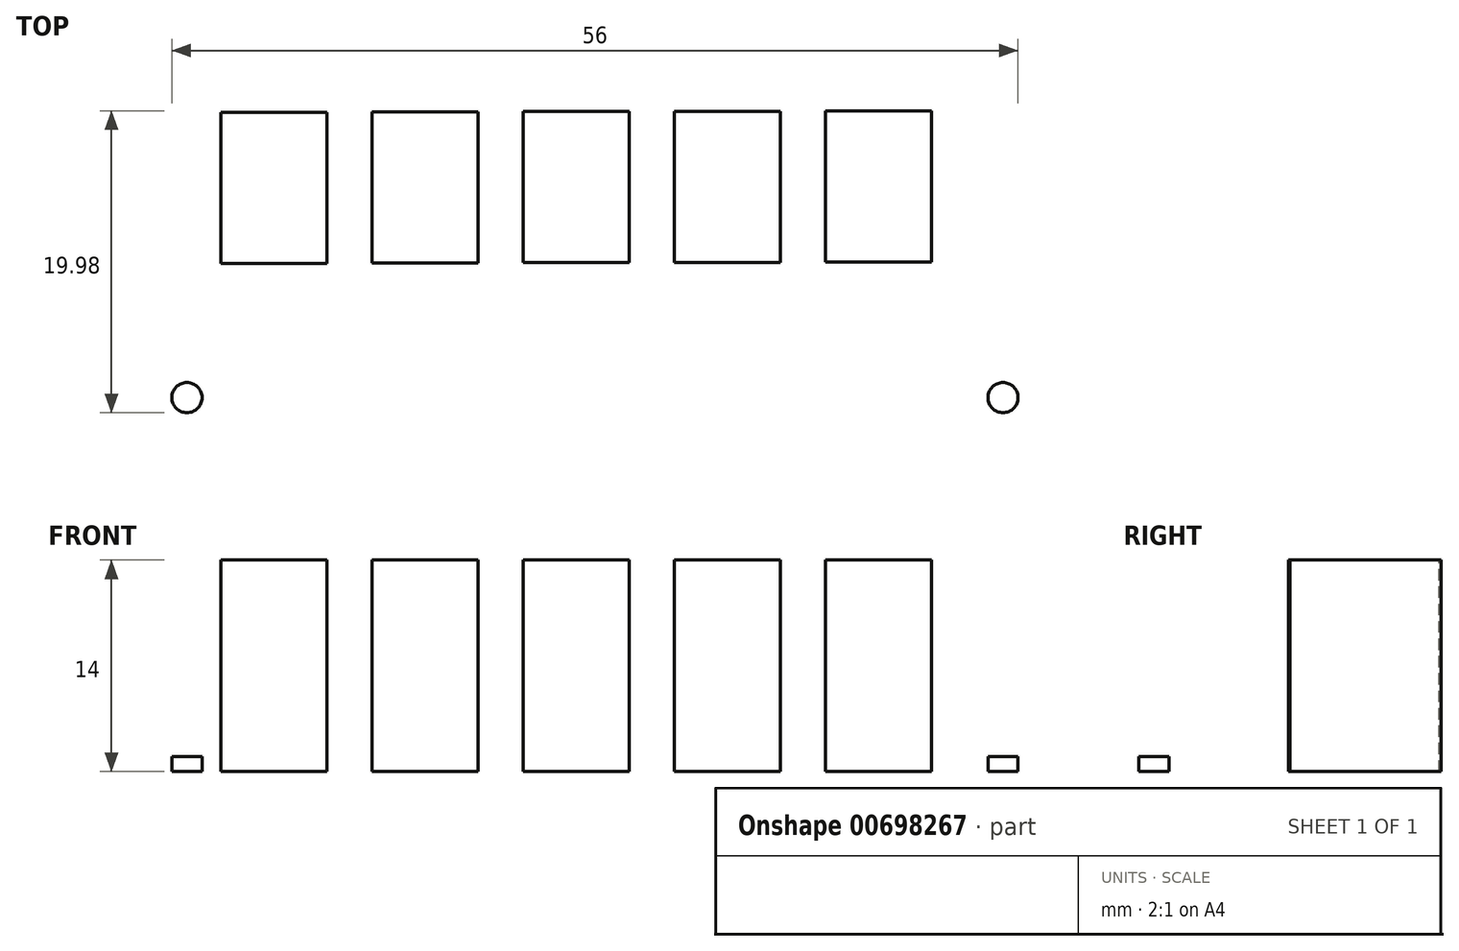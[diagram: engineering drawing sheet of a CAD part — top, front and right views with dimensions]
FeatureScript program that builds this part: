
annotation { "Feature Type Name" : "Feature", "Feature Type Description" : "" }
export const myFeature = defineFeature(function(context is Context, id is Id, definition is map)
    precondition{}
    {
        {
            var Q0;
            Q0=qCreatedBy(makeId("Top.planeOp"),FACE);
            var sketch = newSketch(context, id + "F0", { "sketchPlane" : qUnion([Q0])});
            skLineSegment(sketch, "E0.bottom", {"start": v(29, 19.5) * mm, "end": v(-29, 19.5) * mm});
            skLineSegment(sketch, "E0.top", {"start": v(29, -19.5) * mm, "end": v(-29, -19.5) * mm});
            skLineSegment(sketch, "E0.left", {"start": v(29, 19.5) * mm, "end": v(29, -19.5) * mm});
            skLineSegment(sketch, "E0.right", {"start": v(-29, 19.5) * mm, "end": v(-29, -19.5) * mm});
            skPoint(sketch, "E0.middle", {"position": v(0, 0) * mm});
            skSolve(sketch);
        }
        {
            var Q0;
            Q0 = qSketchRegion(id + "F0", true);
            extrude(context, id + "F1", {"entities" : qUnion([Q0]), "depth" : 14 * mm, "offsetDistance" : 25.4 * mm});
        }
        {
            var Q0;
            Q0=makeQuery(id+"F1.opExtrude","CAP_FACE",FACE,{"disambiguationData":[OSD([sQuery(id+"F0.wireOp",EDGE,"E0.bottom"),sQuery(id+"F0.wireOp",EDGE,"E0.top"),sQuery(id+"F0.wireOp",EDGE,"E0.left"),sQuery(id+"F0.wireOp",EDGE,"E0.right")])],"isStart":false});
            var sketch = newSketch(context, id + "F2", { "sketchPlane" : qUnion([Q0])});
            skLineSegment(sketch, "E1.bottom", {"start": v(-17.74, -8.62) * mm, "end": v(-24.74, -8.62) * mm});
            skLineSegment(sketch, "E1.top", {"start": v(-17.74, 1.38) * mm, "end": v(-24.74, 1.38) * mm});
            skLineSegment(sketch, "E1.left", {"start": v(-17.74, -8.62) * mm, "end": v(-17.74, 1.38) * mm});
            skLineSegment(sketch, "E1.right", {"start": v(-24.74, -8.62) * mm, "end": v(-24.74, 1.38) * mm});
            skPoint(sketch, "E1.middle", {"position": v(-21.24, -3.62) * mm});
            skLineSegment(sketch, "E2.1.0.0", {"start": v(-7.74, -8.6) * mm, "end": v(-7.74, 1.4) * mm});
            skLineSegment(sketch, "E2.1.0.1", {"start": v(-7.74, 1.4) * mm, "end": v(-14.74, 1.4) * mm});
            skLineSegment(sketch, "E2.1.0.2", {"start": v(-14.74, -8.6) * mm, "end": v(-14.74, 1.4) * mm});
            skLineSegment(sketch, "E2.1.0.3", {"start": v(-7.74, -8.6) * mm, "end": v(-14.74, -8.6) * mm});
            skLineSegment(sketch, "E2.2.0.0", {"start": v(2.26, -8.57) * mm, "end": v(2.26, 1.43) * mm});
            skLineSegment(sketch, "E2.2.0.1", {"start": v(2.26, 1.43) * mm, "end": v(-4.74, 1.43) * mm});
            skLineSegment(sketch, "E2.2.0.2", {"start": v(-4.74, -8.57) * mm, "end": v(-4.74, 1.43) * mm});
            skLineSegment(sketch, "E2.2.0.3", {"start": v(2.26, -8.57) * mm, "end": v(-4.74, -8.57) * mm});
            skLineSegment(sketch, "E2.3.0.0", {"start": v(12.26, -8.54) * mm, "end": v(12.26, 1.46) * mm});
            skLineSegment(sketch, "E2.3.0.1", {"start": v(12.26, 1.46) * mm, "end": v(5.26, 1.46) * mm});
            skLineSegment(sketch, "E2.3.0.2", {"start": v(5.26, -8.54) * mm, "end": v(5.26, 1.46) * mm});
            skLineSegment(sketch, "E2.3.0.3", {"start": v(12.26, -8.54) * mm, "end": v(5.26, -8.54) * mm});
            skLineSegment(sketch, "E2.4.0.0", {"start": v(22.26, -8.52) * mm, "end": v(22.26, 1.48) * mm});
            skLineSegment(sketch, "E2.4.0.1", {"start": v(22.26, 1.48) * mm, "end": v(15.26, 1.48) * mm});
            skLineSegment(sketch, "E2.4.0.2", {"start": v(15.26, -8.52) * mm, "end": v(15.26, 1.48) * mm});
            skLineSegment(sketch, "E2.4.0.3", {"start": v(22.26, -8.52) * mm, "end": v(15.26, -8.52) * mm});
            skLineSegment(sketch, "E2.direction1", {"start": v(-17.74, -8.62) * mm, "end": v(-7.74, -8.6) * mm, "construction": true});
            skSolve(sketch);
        }
        {
            var Q0;
            Q0=makeQuery(id+"F2.imprint","IMPRINT",FACE,{"disambiguationData":[TD([[makeQuery(id+"F2.imprint","IMPRINT",EDGE,{"derivedFrom":sQuery(id+"F2.wireOp",EDGE,"E1.bottom")}),1.0]])]});
            extrude(context, id + "F3", {"entities" : qUnion([Q0]), "operationType" : NewBodyOperationType.REMOVE, "oppositeDirection" : true, "depth" : 13 * mm, "offsetDistance" : 25 * mm});
        }
        {
            var Q0;
            Q0=makeQuery(id+"F3.boolean.opBoolean","COPY",FACE,{"derivedFrom":makeQuery(id+"F3.opExtrude","CAP_FACE",FACE,{"disambiguationData":[OSD([sQuery(id+"F0.wireOp",EDGE,"E0.bottom"),sQuery(id+"F0.wireOp",EDGE,"E0.top"),sQuery(id+"F0.wireOp",EDGE,"E0.left"),sQuery(id+"F0.wireOp",EDGE,"E0.right"),sQuery(id+"F2.wireOp",EDGE,"E1.bottom"),sQuery(id+"F2.wireOp",EDGE,"E1.top"),sQuery(id+"F2.wireOp",EDGE,"E1.left"),sQuery(id+"F2.wireOp",EDGE,"E1.right"),sQuery(id+"F2.wireOp",EDGE,"E2.1.0.0"),sQuery(id+"F2.wireOp",EDGE,"E2.1.0.1"),sQuery(id+"F2.wireOp",EDGE,"E2.1.0.2"),sQuery(id+"F2.wireOp",EDGE,"E2.1.0.3"),sQuery(id+"F2.wireOp",EDGE,"E2.2.0.0"),sQuery(id+"F2.wireOp",EDGE,"E2.2.0.1"),sQuery(id+"F2.wireOp",EDGE,"E2.2.0.2"),sQuery(id+"F2.wireOp",EDGE,"E2.2.0.3"),sQuery(id+"F2.wireOp",EDGE,"E2.3.0.0"),sQuery(id+"F2.wireOp",EDGE,"E2.3.0.1"),sQuery(id+"F2.wireOp",EDGE,"E2.3.0.2"),sQuery(id+"F2.wireOp",EDGE,"E2.3.0.3"),sQuery(id+"F2.wireOp",EDGE,"E2.4.0.0"),sQuery(id+"F2.wireOp",EDGE,"E2.4.0.1"),sQuery(id+"F2.wireOp",EDGE,"E2.4.0.2"),sQuery(id+"F2.wireOp",EDGE,"E2.4.0.3")])],"isStart":false})});
            var sketch = newSketch(context, id + "F4", { "sketchPlane" : qUnion([Q0])});
            skCircle(sketch, "E3", {"center": v(-27, 17.5) * mm, "radius": 1 * mm});
            skCircle(sketch, "E4.MirrorC", {"center": v(-27, -17.5) * mm, "radius": 1 * mm});
            skCircle(sketch, "E5.1.0.0", {"center": v(27, 17.5) * mm, "radius": 1 * mm});
            skCircle(sketch, "E5.1.0.1", {"center": v(27, -17.5) * mm, "radius": 1 * mm});
            skLineSegment(sketch, "E5.direction1", {"start": v(-27, -17.5) * mm, "end": v(27, -17.5) * mm, "construction": true});
            skSolve(sketch);
        }
        {
            var Q0;
            Q0=makeQuery(id+"F4.imprint","IMPRINT",FACE,{"disambiguationData":[TD([[makeQuery(id+"F4.imprint","IMPRINT",EDGE,{"derivedFrom":sQuery(id+"F4.wireOp",EDGE,"E3")}),1.0]])]});
            var Q1;
            Q1=makeQuery(id+"F4.imprint","IMPRINT",FACE,{"disambiguationData":[TD([[makeQuery(id+"F4.imprint","IMPRINT",EDGE,{"derivedFrom":sQuery(id+"F4.wireOp",EDGE,"E4.MirrorC")}),-1.0]])]});
            var Q2;
            Q2=makeQuery(id+"F4.imprint","IMPRINT",FACE,{"disambiguationData":[TD([[makeQuery(id+"F4.imprint","IMPRINT",EDGE,{"derivedFrom":sQuery(id+"F4.wireOp",EDGE,"E5.1.0.1")}),-1.0]])]});
            var Q3;
            Q3=makeQuery(id+"F4.imprint","IMPRINT",FACE,{"disambiguationData":[TD([[makeQuery(id+"F4.imprint","IMPRINT",EDGE,{"derivedFrom":sQuery(id+"F4.wireOp",EDGE,"E5.1.0.0")}),1.0]])]});
            extrude(context, id + "F5", {"entities" : qUnion([Q0, Q1, Q2, Q3]), "operationType" : NewBodyOperationType.REMOVE, "oppositeDirection" : true, "depth" : 25 * mm, "offsetDistance" : 25 * mm});
        }
    });
